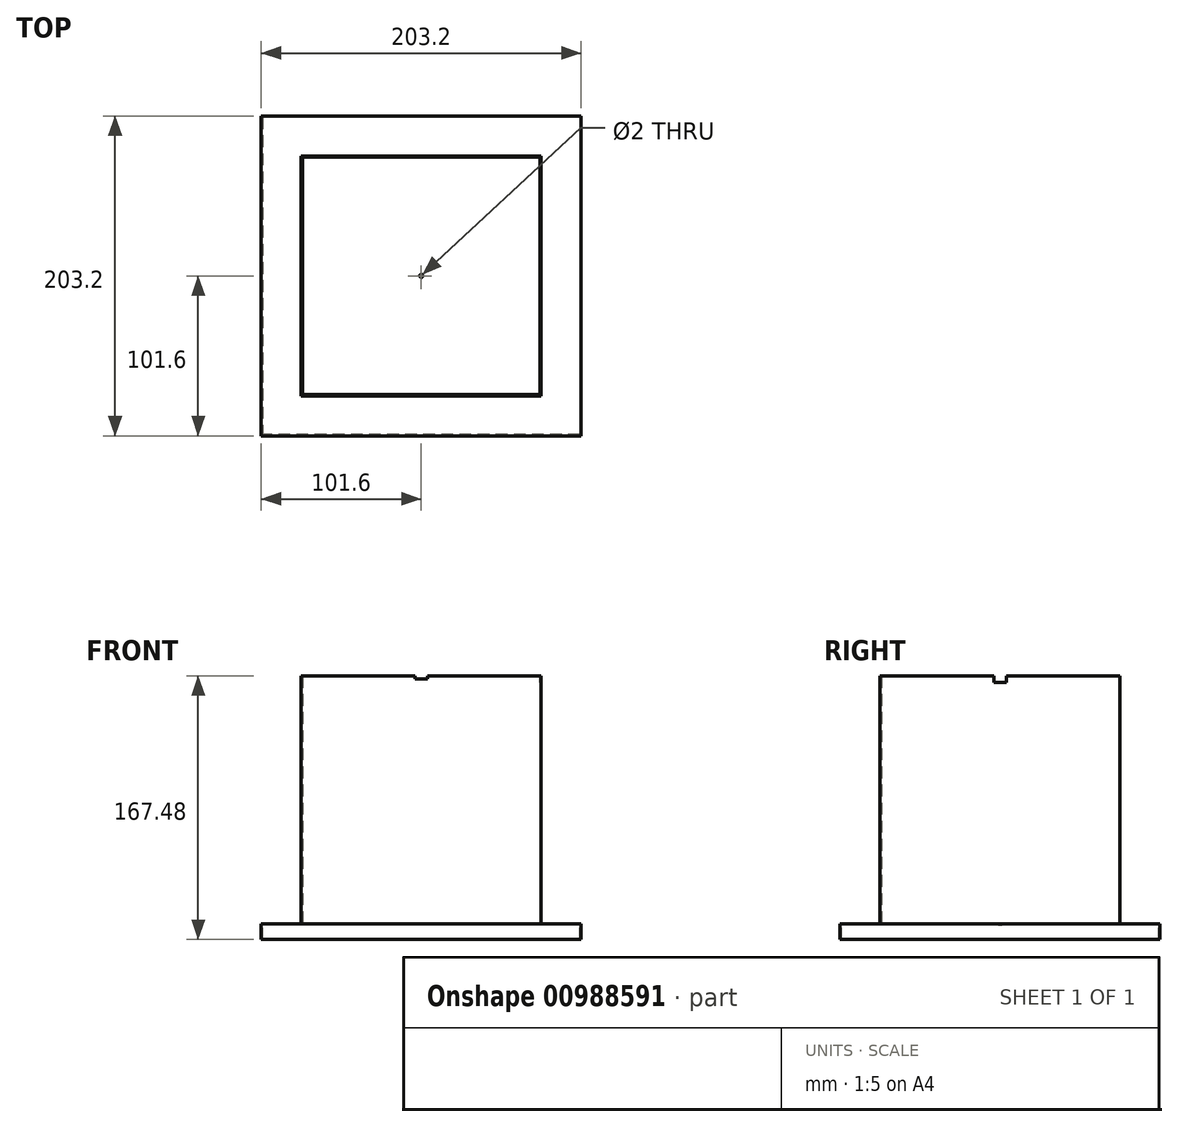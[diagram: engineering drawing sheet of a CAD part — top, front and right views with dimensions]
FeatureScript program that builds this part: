
annotation { "Feature Type Name" : "Feature", "Feature Type Description" : "" }
export const myFeature = defineFeature(function(context is Context, id is Id, definition is map)
    precondition{}
    {
        {
            var Q0;
            Q0=qCreatedBy(makeId("Top.planeOp"),FACE);
            var sketch = newSketch(context, id + "F0", { "sketchPlane" : qUnion([Q0])});
            skLineSegment(sketch, "E0.bottom", {"start": v(101.6, 101.6) * mm, "end": v(-101.6, 101.6) * mm});
            skLineSegment(sketch, "E0.top", {"start": v(101.6, -101.6) * mm, "end": v(-101.6, -101.6) * mm});
            skLineSegment(sketch, "E0.left", {"start": v(101.6, 101.6) * mm, "end": v(101.6, -101.6) * mm});
            skLineSegment(sketch, "E0.right", {"start": v(-101.6, 101.6) * mm, "end": v(-101.6, -101.6) * mm});
            skPoint(sketch, "E0.middle", {"position": v(0, 0) * mm});
            skCircle(sketch, "E1", {"center": v(0, 0) * mm, "radius": 1 * mm});
            skSolve(sketch);
        }
        {
            var Q0;
            Q0=makeQuery(id+"F0.imprint","IMPRINT",FACE,{"disambiguationData":[TD([[makeQuery(id+"F0.imprint","IMPRINT",EDGE,{"derivedFrom":sQuery(id+"F0.wireOp",EDGE,"E0.bottom")}),1.0]])]});
            extrude(context, id + "F1", {"entities" : qUnion([Q0]), "depth" : 0.8 * mm, "offsetDistance" : 25.4 * mm});
        }
        {
            var Q0;
            Q0=makeQuery(id+"F1.opExtrude","CAP_FACE",FACE,{"disambiguationData":[OSD([sQuery(id+"F0.wireOp",EDGE,"E0.bottom"),sQuery(id+"F0.wireOp",EDGE,"E0.top"),sQuery(id+"F0.wireOp",EDGE,"E0.left"),sQuery(id+"F0.wireOp",EDGE,"E0.right")])],"isStart":true});
            var sketch = newSketch(context, id + "F2", { "sketchPlane" : qUnion([Q0])});
            skLineSegment(sketch, "E2.0", {"start": v(-101.6, -101.6) * mm, "end": v(-101.6, 101.6) * mm});
            skLineSegment(sketch, "E2.1", {"start": v(101.6, 101.6) * mm, "end": v(-101.6, 101.6) * mm});
            skLineSegment(sketch, "E2.2", {"start": v(101.6, -101.6) * mm, "end": v(101.6, 101.6) * mm});
            skLineSegment(sketch, "E2.3", {"start": v(101.6, -101.6) * mm, "end": v(-101.6, -101.6) * mm});
            skLineSegment(sketch, "E3.0", {"start": v(-100.8, -100.8) * mm, "end": v(-100.8, 100.8) * mm});
            skLineSegment(sketch, "E3.1", {"start": v(100.8, -100.8) * mm, "end": v(-100.8, -100.8) * mm});
            skLineSegment(sketch, "E3.2", {"start": v(100.8, -100.8) * mm, "end": v(100.8, 100.8) * mm});
            skLineSegment(sketch, "E3.3", {"start": v(100.8, 100.8) * mm, "end": v(-100.8, 100.8) * mm});
            skSolve(sketch);
        }
        {
            var Q0;
            Q0=qSketchRegion(id+"F2",true);
            extrude(context, id + "F3", {"entities" : qUnion([Q0]), "operationType" : NewBodyOperationType.ADD, "depth" : 9.2 * mm, "offsetDistance" : 25.4 * mm});
        }
        {
            var Q0;
            Q0=makeQuery(id+"F1.opExtrude","CAP_FACE",FACE,{"disambiguationData":[OSD([sQuery(id+"F0.wireOp",EDGE,"E0.bottom"),sQuery(id+"F0.wireOp",EDGE,"E0.top"),sQuery(id+"F0.wireOp",EDGE,"E0.left"),sQuery(id+"F0.wireOp",EDGE,"E0.right")])],"isStart":false});
            var sketch = newSketch(context, id + "F4", { "sketchPlane" : qUnion([Q0])});
            skLineSegment(sketch, "E4.bottom", {"start": v(76.2, 76.2) * mm, "end": v(-76.2, 76.2) * mm});
            skLineSegment(sketch, "E4.top", {"start": v(76.2, -76.2) * mm, "end": v(-76.2, -76.2) * mm});
            skLineSegment(sketch, "E4.left", {"start": v(76.2, 76.2) * mm, "end": v(76.2, -76.2) * mm});
            skLineSegment(sketch, "E4.right", {"start": v(-76.2, 76.2) * mm, "end": v(-76.2, -76.2) * mm});
            skPoint(sketch, "E4.middle", {"position": v(0, 0) * mm});
            skLineSegment(sketch, "E5.0", {"start": v(-75.4, 75.4) * mm, "end": v(-75.4, -75.4) * mm});
            skLineSegment(sketch, "E5.1", {"start": v(75.4, 75.4) * mm, "end": v(-75.4, 75.4) * mm});
            skLineSegment(sketch, "E5.2", {"start": v(75.4, 75.4) * mm, "end": v(75.4, -75.4) * mm});
            skLineSegment(sketch, "E5.3", {"start": v(75.4, -75.4) * mm, "end": v(-75.4, -75.4) * mm});
            skSolve(sketch);
        }
        {
            var Q0;
            Q0=qSketchRegion(id+"F4",true);
            extrude(context, id + "F5", {"entities" : qUnion([Q0]), "depth" : 157.48 * mm, "offsetDistance" : 25.4 * mm});
        }
        {
            var Q0;
            Q0=makeQuery(id+"F5.opExtrude","SWEPT_FACE",FACE,{"disambiguationData":[OSD([sQuery(id+"F4.wireOp",EDGE,"E4.top")])]});
            var sketch = newSketch(context, id + "F6", { "sketchPlane" : qUnion([Q0])});
            skLineSegment(sketch, "E6", {"start": v(-4, 158.28) * mm, "end": v(4, 158.28) * mm});
            skLineSegment(sketch, "E7", {"start": v(-4, 158.28) * mm, "end": v(-4, 156.28) * mm});
            skLineSegment(sketch, "E8", {"start": v(4, 158.28) * mm, "end": v(4, 156.28) * mm});
            skLineSegment(sketch, "E9", {"start": v(4, 156.28) * mm, "end": v(-4, 156.28) * mm});
            skSolve(sketch);
        }
        {
            var Q0;
            Q0=makeQuery(id+"F6.imprint","IMPRINT",FACE,{"disambiguationData":[TD([[makeQuery(id+"F6.imprint","IMPRINT",EDGE,{"derivedFrom":sQuery(id+"F6.wireOp",EDGE,"E6")}),1.0]])]});
            extrude(context, id + "F7", {"entities" : qUnion([Q0]), "operationType" : NewBodyOperationType.REMOVE, "endBound" : BoundingType.THROUGH_ALL, "oppositeDirection" : true, "depth" : 25.4 * mm, "offsetDistance" : 25.4 * mm});
        }
        {
            var Q0;
            Q0=makeQuery(id+"F5.opExtrude","SWEPT_FACE",FACE,{"disambiguationData":[OSD([sQuery(id+"F4.wireOp",EDGE,"E4.right")])]});
            var sketch = newSketch(context, id + "F8", { "sketchPlane" : qUnion([Q0])});
            skLineSegment(sketch, "E10", {"start": v(-4, 158.28) * mm, "end": v(4, 158.28) * mm});
            skLineSegment(sketch, "E11", {"start": v(-4, 158.28) * mm, "end": v(-4, 154.28) * mm});
            skLineSegment(sketch, "E12", {"start": v(4, 158.28) * mm, "end": v(4, 154.28) * mm});
            skLineSegment(sketch, "E13", {"start": v(4, 154.28) * mm, "end": v(-4, 154.28) * mm});
            skSolve(sketch);
        }
        {
            var Q0;
            Q0=qSketchRegion(id+"F8",true);
            extrude(context, id + "F9", {"entities" : qUnion([Q0]), "operationType" : NewBodyOperationType.REMOVE, "endBound" : BoundingType.THROUGH_ALL, "oppositeDirection" : true, "depth" : 25.4 * mm, "offsetDistance" : 25.4 * mm});
        }
    });
